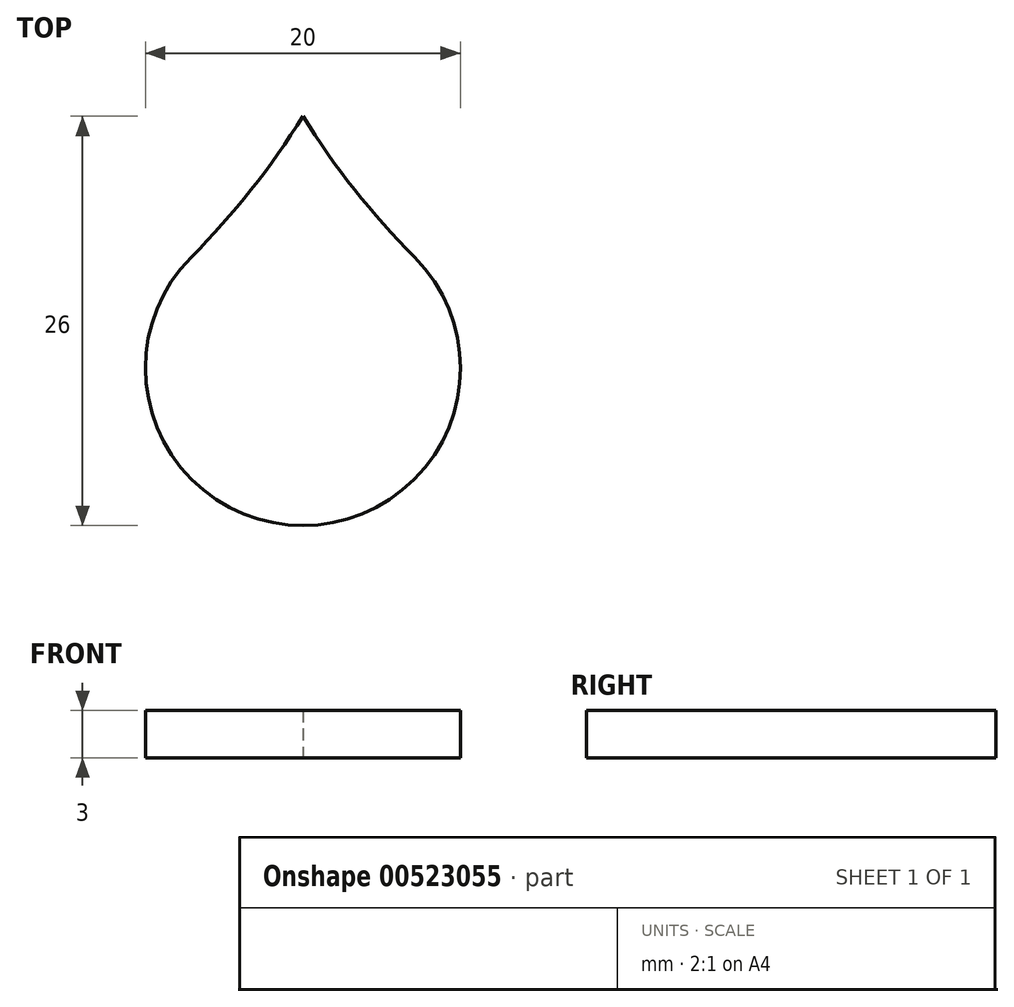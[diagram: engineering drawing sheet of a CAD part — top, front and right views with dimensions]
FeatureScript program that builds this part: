
annotation { "Feature Type Name" : "Feature", "Feature Type Description" : "" }
export const myFeature = defineFeature(function(context is Context, id is Id, definition is map)
    precondition{}
    {
        {
            var Q0;
            Q0=qCreatedBy(makeId("Top.planeOp"),FACE);
            var sketch = newSketch(context, id + "F0", { "sketchPlane" : qUnion([Q0])});
            skArc(sketch, "E0", {"start": v(-7.08, 7.06) * mm, "mid": v(0, -10) * mm, "end": v(7.08, 7.06) * mm});
            skArc(sketch, "E1", {"start": v(-7.08, 7.06) * mm, "mid": v(-3.28, 11.33) * mm, "end": v(0, 16) * mm});
            skArc(sketch, "E2.MirrorCS", {"start": v(7.08, 7.06) * mm, "mid": v(3.28, 11.33) * mm, "end": v(0, 16) * mm});
            skLineSegment(sketch, "E3", {"start": v(0, 69.87) * mm, "end": v(0, -69.35) * mm, "construction": true});
            skLineSegment(sketch, "E4", {"start": v(-62.95, 0) * mm, "end": v(53.54, 0) * mm, "construction": true});
            skPoint(sketch, "E5", {"position": v(-119.63, -30.68) * mm});
            skPoint(sketch, "E6", {"position": v(0, 18) * mm});
            skLineSegment(sketch, "E7", {"start": v(0, 18) * mm, "end": v(-52.73, 48.44) * mm, "construction": true});
            skLineSegment(sketch, "E8", {"start": v(2.37, 18) * mm, "end": v(46.41, 43.43) * mm, "construction": true});
            skSolve(sketch);
        }
        {
            var Q0;
            Q0 = qSketchRegion(id + "F0", true);
            extrude(context, id + "F1", {"entities" : qUnion([Q0]), "depth" : 3 * mm, "offsetDistance" : 25 * mm});
        }
    });
